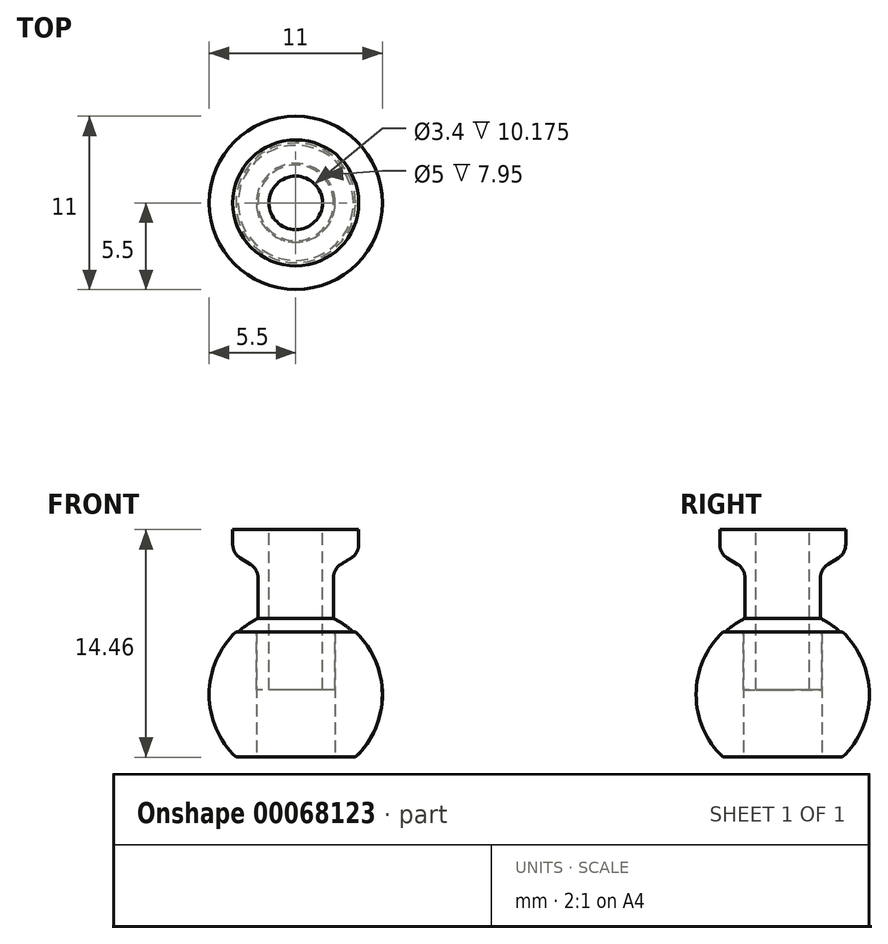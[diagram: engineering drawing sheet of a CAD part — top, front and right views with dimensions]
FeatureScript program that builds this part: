
annotation { "Feature Type Name" : "Feature", "Feature Type Description" : "" }
export const myFeature = defineFeature(function(context is Context, id is Id, definition is map)
    precondition{}
    {
        {
            var Q0;
            Q0=qCreatedBy(makeId("Front.planeOp"),FACE);
            var sketch = newSketch(context, id + "F0", { "sketchPlane" : qUnion([Q0])});
            skArc(sketch, "E0", {"start": v(-3.8, 3.97) * mm, "mid": v(-5.5, 0) * mm, "end": v(-3.8, -3.98) * mm});
            skLineSegment(sketch, "E1", {"start": v(0, 3.98) * mm, "end": v(0, -3.98) * mm});
            skLineSegment(sketch, "E2", {"start": v(0, 3.98) * mm, "end": v(-3.8, 3.98) * mm});
            skLineSegment(sketch, "E3", {"start": v(0, -3.98) * mm, "end": v(-3.8, -3.98) * mm});
            skSolve(sketch);
        }
        {
            var Q0;
            Q0 = qSketchRegion(id + "F0", true);
            var Q1;
            Q1=sQuery(id+"F0.wireOp",EDGE,"E1");
            revolve(context, id + "F1", {"entities" : qUnion([Q0]), "axis" : qUnion([Q1]), "revolveType" : RevolveType.FULL});
        }
        {
            var Q0;
            Q0=makeQuery(id+"F1.opRevolve","SWEPT_FACE",FACE,{"disambiguationData":[OSD([sQuery(id+"F0.wireOp",EDGE,"E3")])]});
            var sketch = newSketch(context, id + "F2", { "sketchPlane" : qUnion([Q0])});
            skCircle(sketch, "E4", {"center": v(0, 0) * mm, "radius": 2.5 * mm});
            skSolve(sketch);
        }
        {
            var Q0;
            Q0=makeQuery(id+"F2.imprint","IMPRINT",FACE,{"disambiguationData":[TD([[makeQuery(id+"F2.imprint","IMPRINT",EDGE,{"derivedFrom":sQuery(id+"F2.wireOp",EDGE,"E4")}),1.0]])]});
            var Q1;
            Q1=makeQuery(id+"F1.opRevolve","SWEPT_FACE",FACE,{"disambiguationData":[OSD([sQuery(id+"F0.wireOp",EDGE,"E2")])]});
            extrude(context, id + "F3", {"entities" : qUnion([Q0]), "operationType" : NewBodyOperationType.REMOVE, "endBound" : BoundingType.UP_TO_SURFACE, "oppositeDirection" : true, "endBoundEntityFace" : qUnion([Q1]), "depth" : 25 * mm});
        }
        {
            var Q0;
            Q0=qCreatedBy(makeId("Front.planeOp"),FACE);
            var sketch = newSketch(context, id + "F4", { "sketchPlane" : qUnion([Q0])});
            skLineSegment(sketch, "E5", {"start": v(0, 10.47) * mm, "end": v(0, 0.3) * mm});
            skLineSegment(sketch, "E6", {"start": v(0, 0.3) * mm, "end": v(-2.5, 0.3) * mm});
            skLineSegment(sketch, "E7", {"start": v(-2.5, 0.3) * mm, "end": v(-2.5, 3.98) * mm});
            skLineSegment(sketch, "E8", {"start": v(-2.5, 3.98) * mm, "end": v(-3.66, 3.98) * mm});
            skCircle(sketch, "E9", {"center": v(0, 0) * mm, "radius": 5.4 * mm, "construction": true});
            skLineSegment(sketch, "E10", {"start": v(0, 10.47) * mm, "end": v(-4, 10.47) * mm});
            skLineSegment(sketch, "E11", {"start": v(-4, 10.47) * mm, "end": v(-4, 8.97) * mm});
            skLineSegment(sketch, "E12", {"start": v(-4, 8.97) * mm, "end": v(-2.4, 7.97) * mm});
            skLineSegment(sketch, "E13", {"start": v(-2.4, 7.97) * mm, "end": v(-2.4, 4.84) * mm});
            skArc(sketch, "E14", {"start": v(-2.4, 4.84) * mm, "mid": v(-3.06, 4.45) * mm, "end": v(-3.66, 3.98) * mm});
            skSolve(sketch);
        }
        {
            var Q0;
            Q0=makeQuery(id+"F4.imprint","IMPRINT",FACE,{"disambiguationData":[TD([[makeQuery(id+"F4.imprint","IMPRINT",EDGE,{"derivedFrom":sQuery(id+"F4.wireOp",EDGE,"E5")}),-1.0]])]});
            var Q1;
            Q1=sQuery(id+"F4.wireOp",EDGE,"E5");
            revolve(context, id + "F5", {"entities" : qUnion([Q0]), "axis" : qUnion([Q1]), "revolveType" : RevolveType.FULL});
        }
        {
            var Q0;
            Q0=makeQuery(id+"F5.opRevolve","SWEPT_FACE",FACE,{"disambiguationData":[OSD([sQuery(id+"F4.wireOp",EDGE,"E10")])]});
            var sketch = newSketch(context, id + "F6", { "sketchPlane" : qUnion([Q0])});
            skCircle(sketch, "E15", {"center": v(0, 0) * mm, "radius": 1.7 * mm});
            skSolve(sketch);
        }
        {
            var Q0;
            Q0=makeQuery(id+"F6.imprint","IMPRINT",FACE,{"disambiguationData":[TD([[makeQuery(id+"F6.imprint","IMPRINT",EDGE,{"derivedFrom":sQuery(id+"F6.wireOp",EDGE,"E15")}),1.0]])]});
            var Q1;
            Q1=makeQuery(id+"F5.opRevolve","SWEPT_FACE",FACE,{"disambiguationData":[OSD([sQuery(id+"F4.wireOp",EDGE,"E6")])]});
            extrude(context, id + "F7", {"entities" : qUnion([Q0]), "operationType" : NewBodyOperationType.REMOVE, "endBound" : BoundingType.UP_TO_SURFACE, "oppositeDirection" : true, "endBoundEntityFace" : qUnion([Q1]), "depth" : 25 * mm});
        }
        {
            var Q0;
            Q0=makeQuery(id+"F5.opRevolve","SWEPT_EDGE",EDGE,{"disambiguationData":[OSD([sQuery(id+"F4.wireOp",EDGE,"E12"),sQuery(id+"F4.wireOp",EDGE,"E13")])]});
            fillet(context, id + "F8", {"entities" : qUnion([Q0]), "radius" : 1 * mm, "tangentPropagation" : true, "allowEdgeOverflow" : false});
        }
        {
            var Q0;
            Q0=makeQuery(id+"F5.opRevolve","SWEPT_EDGE",EDGE,{"disambiguationData":[OSD([sQuery(id+"F4.wireOp",EDGE,"E11"),sQuery(id+"F4.wireOp",EDGE,"E12")])]});
            fillet(context, id + "F9", {"entities" : qUnion([Q0]), "radius" : 1 * mm, "tangentPropagation" : true, "allowEdgeOverflow" : false});
        }
    });
